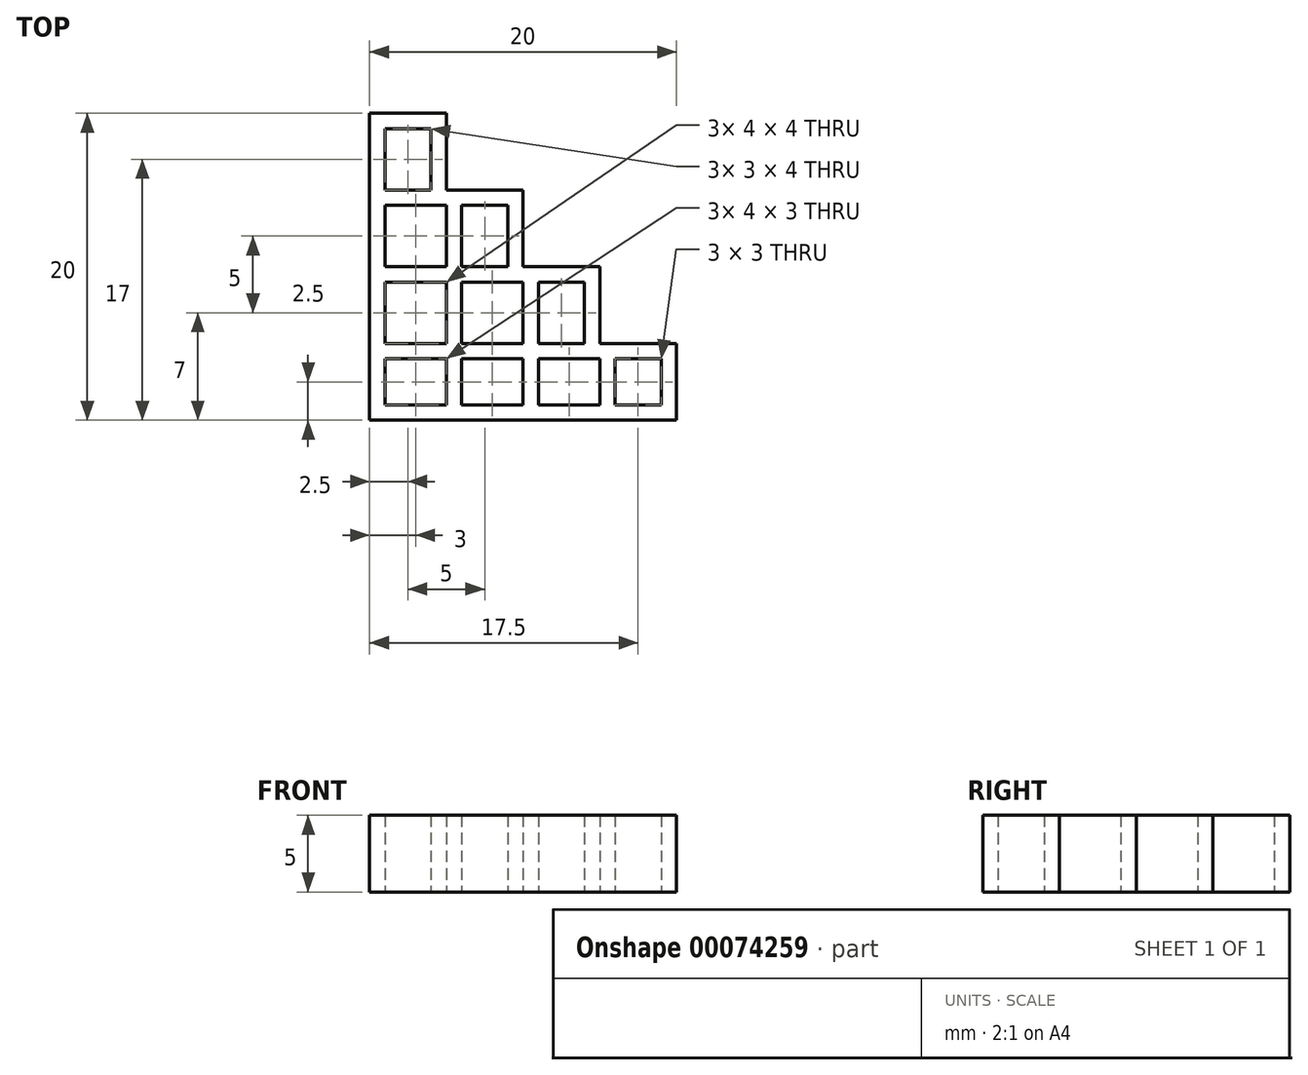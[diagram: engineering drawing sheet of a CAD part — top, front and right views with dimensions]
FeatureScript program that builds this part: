
annotation { "Feature Type Name" : "Feature", "Feature Type Description" : "" }
export const myFeature = defineFeature(function(context is Context, id is Id, definition is map)
    precondition{}
    {
        {
            var Q0;
            Q0=qCreatedBy(makeId("Top.planeOp"),FACE);
            var sketch = newSketch(context, id + "F0", { "sketchPlane" : qUnion([Q0])});
            skLineSegment(sketch, "E0.bottom", {"start": v(0, 0) * mm, "end": v(15, 0) * mm, "construction": true});
            skLineSegment(sketch, "E0.top", {"start": v(0, 10) * mm, "end": v(15, 10) * mm, "construction": true});
            skLineSegment(sketch, "E0.left", {"start": v(0, 0) * mm, "end": v(0, 10) * mm, "construction": true});
            skLineSegment(sketch, "E0.right", {"start": v(15, 0) * mm, "end": v(15, 10) * mm, "construction": true});
            skLineSegment(sketch, "E1.bottom", {"start": v(0, 0) * mm, "end": v(5, 0) * mm, "construction": true});
            skLineSegment(sketch, "E1.top", {"start": v(0, 20) * mm, "end": v(5, 20) * mm, "construction": true});
            skLineSegment(sketch, "E1.left", {"start": v(0, 0) * mm, "end": v(0, 20) * mm, "construction": true});
            skLineSegment(sketch, "E1.right", {"start": v(5, 0) * mm, "end": v(5, 20) * mm, "construction": true});
            skLineSegment(sketch, "E2.bottom", {"start": v(0, 0) * mm, "end": v(10, 0) * mm, "construction": true});
            skLineSegment(sketch, "E2.top", {"start": v(0, 15) * mm, "end": v(10, 15) * mm, "construction": true});
            skLineSegment(sketch, "E2.left", {"start": v(0, 0) * mm, "end": v(0, 15) * mm, "construction": true});
            skLineSegment(sketch, "E2.right", {"start": v(10, 0) * mm, "end": v(10, 15) * mm, "construction": true});
            skLineSegment(sketch, "E3.bottom", {"start": v(0, 0) * mm, "end": v(20, 0) * mm, "construction": true});
            skLineSegment(sketch, "E3.top", {"start": v(0, 5) * mm, "end": v(20, 5) * mm, "construction": true});
            skLineSegment(sketch, "E3.left", {"start": v(0, 0) * mm, "end": v(0, 5) * mm, "construction": true});
            skLineSegment(sketch, "E3.right", {"start": v(20, 0) * mm, "end": v(20, 5) * mm, "construction": true});
            skLineSegment(sketch, "E4", {"start": v(0, 0) * mm, "end": v(0, 20) * mm});
            skLineSegment(sketch, "E5", {"start": v(5, 20) * mm, "end": v(0, 20) * mm});
            skLineSegment(sketch, "E6", {"start": v(5, 20) * mm, "end": v(5, 15) * mm});
            skLineSegment(sketch, "E7", {"start": v(5, 15) * mm, "end": v(10, 15) * mm});
            skLineSegment(sketch, "E8", {"start": v(10, 15) * mm, "end": v(10, 10) * mm});
            skLineSegment(sketch, "E9", {"start": v(10, 10) * mm, "end": v(15, 10) * mm});
            skLineSegment(sketch, "E10", {"start": v(15, 10) * mm, "end": v(15, 5) * mm});
            skLineSegment(sketch, "E11", {"start": v(15, 5) * mm, "end": v(20, 5) * mm});
            skLineSegment(sketch, "E12", {"start": v(20, 5) * mm, "end": v(20, 0) * mm});
            skLineSegment(sketch, "E13", {"start": v(20, 0) * mm, "end": v(0, 0) * mm});
            skLineSegment(sketch, "E14", {"start": v(15, 5) * mm, "end": v(15, 0) * mm});
            skLineSegment(sketch, "E15", {"start": v(10, 10) * mm, "end": v(10, 0) * mm});
            skLineSegment(sketch, "E16", {"start": v(5, 15) * mm, "end": v(5, 0) * mm});
            skLineSegment(sketch, "E17.0", {"start": v(6, 15) * mm, "end": v(6, 0) * mm});
            skLineSegment(sketch, "E18.0", {"start": v(11, 10) * mm, "end": v(11, 0) * mm});
            skLineSegment(sketch, "E19.0", {"start": v(16, 5) * mm, "end": v(16, 0) * mm});
            skLineSegment(sketch, "E20.0", {"start": v(19, 1) * mm, "end": v(1, 1) * mm});
            skLineSegment(sketch, "E20.1", {"start": v(19, 4) * mm, "end": v(19, 1) * mm});
            skLineSegment(sketch, "E20.2", {"start": v(1, 1) * mm, "end": v(1, 19) * mm});
            skLineSegment(sketch, "E20.3", {"start": v(14, 4) * mm, "end": v(19, 4) * mm});
            skLineSegment(sketch, "E20.4", {"start": v(14, 9) * mm, "end": v(14, 4) * mm});
            skLineSegment(sketch, "E20.5", {"start": v(9, 9) * mm, "end": v(14, 9) * mm});
            skLineSegment(sketch, "E20.6", {"start": v(4, 19) * mm, "end": v(1, 19) * mm});
            skLineSegment(sketch, "E20.7", {"start": v(4, 19) * mm, "end": v(4, 14) * mm});
            skLineSegment(sketch, "E20.8", {"start": v(4, 14) * mm, "end": v(9, 14) * mm});
            skLineSegment(sketch, "E20.9", {"start": v(9, 14) * mm, "end": v(9, 9) * mm});
            skLineSegment(sketch, "E21", {"start": v(1, 15) * mm, "end": v(4, 15) * mm});
            skLineSegment(sketch, "E22", {"start": v(1, 10) * mm, "end": v(9, 10) * mm});
            skLineSegment(sketch, "E23", {"start": v(1, 5) * mm, "end": v(14, 5) * mm});
            skLineSegment(sketch, "E24.0", {"start": v(1, 14) * mm, "end": v(4, 14) * mm});
            skLineSegment(sketch, "E25.0", {"start": v(1, 9) * mm, "end": v(9, 9) * mm});
            skLineSegment(sketch, "E26.0", {"start": v(1, 4) * mm, "end": v(14, 4) * mm});
            skSolve(sketch);
        }
        {
            var Q0;
            {var subQ18=sQuery(id+"F0.wireOp",EDGE,"E4");Q0=makeQuery(id+"F0.imprint","IMPRINT",FACE,{"disambiguationData":[TD([[makeQuery(id+"F0.imprint","IMPRINT",EDGE,{"derivedFrom":subQ18}),-1.0]])]});}
            var Q1;
            {var subQ1=sQuery(id+"F0.wireOp",EDGE,"E7");var subQ3=sQuery(id+"F0.wireOp",EDGE,"E17.0");var subQ4=makeQuery(id+"F0.imprint","INTERSECT",VERTEX,{"derivedFrom":[subQ1,subQ3]});Q1=makeQuery(id+"F0.imprint","IMPRINT",FACE,{"disambiguationData":[TD([[makeQuery(id+"F0.imprint","IMPRINT",EDGE,{"disambiguationData":[TD([[subQ4,-1.0]])],"derivedFrom":subQ3}),-1.0]])]});}
            var Q2;
            {var subQ6=sQuery(id+"F0.wireOp",EDGE,"E8");Q2=makeQuery(id+"F0.imprint","IMPRINT",FACE,{"disambiguationData":[TD([[makeQuery(id+"F0.imprint","IMPRINT",EDGE,{"derivedFrom":subQ6}),-1.0]])]});}
            var Q3;
            {var subQ1=sQuery(id+"F0.wireOp",EDGE,"E9");var subQ3=sQuery(id+"F0.wireOp",EDGE,"E18.0");var subQ4=makeQuery(id+"F0.imprint","INTERSECT",VERTEX,{"derivedFrom":[subQ1,subQ3]});Q3=makeQuery(id+"F0.imprint","IMPRINT",FACE,{"disambiguationData":[TD([[makeQuery(id+"F0.imprint","IMPRINT",EDGE,{"disambiguationData":[TD([[subQ4,-1.0]])],"derivedFrom":subQ3}),-1.0]])]});}
            var Q4;
            {var subQ10=sQuery(id+"F0.wireOp",EDGE,"E10");Q4=makeQuery(id+"F0.imprint","IMPRINT",FACE,{"disambiguationData":[TD([[makeQuery(id+"F0.imprint","IMPRINT",EDGE,{"derivedFrom":subQ10}),-1.0]])]});}
            var Q5;
            {var subQ0=sQuery(id+"F0.wireOp",EDGE,"E20.5");var subQ1=sQuery(id+"F0.wireOp",EDGE,"E15");var subQ2=makeQuery(id+"F0.imprint","INTERSECT",VERTEX,{"derivedFrom":[subQ1,subQ0]});Q5=makeQuery(id+"F0.imprint","IMPRINT",FACE,{"disambiguationData":[TD([[makeQuery(id+"F0.imprint","IMPRINT",EDGE,{"disambiguationData":[TD([[subQ2,-1.0]])],"derivedFrom":subQ1}),1.0]])]});}
            var Q6;
            {var subQ0=sQuery(id+"F0.wireOp",EDGE,"E22");var subQ1=sQuery(id+"F0.wireOp",EDGE,"E16");var subQ2=makeQuery(id+"F0.imprint","INTERSECT",VERTEX,{"derivedFrom":[subQ1,subQ0]});Q6=makeQuery(id+"F0.imprint","IMPRINT",FACE,{"disambiguationData":[TD([[makeQuery(id+"F0.imprint","IMPRINT",EDGE,{"disambiguationData":[TD([[subQ2,-1.0]])],"derivedFrom":subQ1}),1.0]])]});}
            var Q7;
            {var subQ0=sQuery(id+"F0.wireOp",EDGE,"E20.8");var subQ1=sQuery(id+"F0.wireOp",EDGE,"E16");var subQ2=makeQuery(id+"F0.imprint","INTERSECT",VERTEX,{"derivedFrom":[subQ1,subQ0]});Q7=makeQuery(id+"F0.imprint","IMPRINT",FACE,{"disambiguationData":[TD([[makeQuery(id+"F0.imprint","IMPRINT",EDGE,{"disambiguationData":[TD([[subQ2,-1.0]])],"derivedFrom":subQ1}),1.0]])]});}
            var Q8;
            {var subQ0=sQuery(id+"F0.wireOp",EDGE,"E22");var subQ1=sQuery(id+"F0.wireOp",EDGE,"E16");var subQ2=makeQuery(id+"F0.imprint","INTERSECT",VERTEX,{"derivedFrom":[subQ1,subQ0]});Q8=makeQuery(id+"F0.imprint","IMPRINT",FACE,{"disambiguationData":[TD([[makeQuery(id+"F0.imprint","IMPRINT",EDGE,{"disambiguationData":[TD([[subQ2,-1.0]])],"derivedFrom":subQ1}),-1.0]])]});}
            var Q9;
            {var subQ0=sQuery(id+"F0.wireOp",EDGE,"E25.0");var subQ1=sQuery(id+"F0.wireOp",EDGE,"E16");var subQ2=makeQuery(id+"F0.imprint","INTERSECT",VERTEX,{"derivedFrom":[subQ1,subQ0]});Q9=makeQuery(id+"F0.imprint","IMPRINT",FACE,{"disambiguationData":[TD([[makeQuery(id+"F0.imprint","IMPRINT",EDGE,{"disambiguationData":[TD([[subQ2,-1.0]])],"derivedFrom":subQ1}),1.0]])]});}
            var Q10;
            {var subQ0=sQuery(id+"F0.wireOp",EDGE,"E23");var subQ1=sQuery(id+"F0.wireOp",EDGE,"E16");var subQ2=makeQuery(id+"F0.imprint","INTERSECT",VERTEX,{"derivedFrom":[subQ1,subQ0]});Q10=makeQuery(id+"F0.imprint","IMPRINT",FACE,{"disambiguationData":[TD([[makeQuery(id+"F0.imprint","IMPRINT",EDGE,{"disambiguationData":[TD([[subQ2,-1.0]])],"derivedFrom":subQ1}),-1.0]])]});}
            var Q11;
            {var subQ0=sQuery(id+"F0.wireOp",EDGE,"E26.0");var subQ1=sQuery(id+"F0.wireOp",EDGE,"E16");var subQ2=makeQuery(id+"F0.imprint","INTERSECT",VERTEX,{"derivedFrom":[subQ1,subQ0]});Q11=makeQuery(id+"F0.imprint","IMPRINT",FACE,{"disambiguationData":[TD([[makeQuery(id+"F0.imprint","IMPRINT",EDGE,{"disambiguationData":[TD([[subQ2,-1.0]])],"derivedFrom":subQ1}),1.0]])]});}
            var Q12;
            {var subQ0=sQuery(id+"F0.wireOp",EDGE,"E23");var subQ1=sQuery(id+"F0.wireOp",EDGE,"E16");var subQ2=makeQuery(id+"F0.imprint","INTERSECT",VERTEX,{"derivedFrom":[subQ1,subQ0]});Q12=makeQuery(id+"F0.imprint","IMPRINT",FACE,{"disambiguationData":[TD([[makeQuery(id+"F0.imprint","IMPRINT",EDGE,{"disambiguationData":[TD([[subQ2,-1.0]])],"derivedFrom":subQ1}),1.0]])]});}
            var Q13;
            {var subQ0=sQuery(id+"F0.wireOp",EDGE,"E16");var subQ1=sQuery(id+"F0.wireOp",EDGE,"E13");var subQ2=makeQuery(id+"F0.imprint","INTERSECT",VERTEX,{"derivedFrom":[subQ1,subQ0]});Q13=makeQuery(id+"F0.imprint","IMPRINT",FACE,{"disambiguationData":[TD([[makeQuery(id+"F0.imprint","IMPRINT",EDGE,{"disambiguationData":[TD([[subQ2,1.0]])],"derivedFrom":subQ1}),-1.0]])]});}
            var Q14;
            {var subQ0=sQuery(id+"F0.wireOp",EDGE,"E15");var subQ1=sQuery(id+"F0.wireOp",EDGE,"E13");var subQ2=makeQuery(id+"F0.imprint","INTERSECT",VERTEX,{"derivedFrom":[subQ1,subQ0]});Q14=makeQuery(id+"F0.imprint","IMPRINT",FACE,{"disambiguationData":[TD([[makeQuery(id+"F0.imprint","IMPRINT",EDGE,{"disambiguationData":[TD([[subQ2,-1.0]])],"derivedFrom":subQ1}),-1.0]])]});}
            var Q15;
            {var subQ0=sQuery(id+"F0.wireOp",EDGE,"E23");var subQ1=sQuery(id+"F0.wireOp",EDGE,"E15");var subQ2=makeQuery(id+"F0.imprint","INTERSECT",VERTEX,{"derivedFrom":[subQ1,subQ0]});Q15=makeQuery(id+"F0.imprint","IMPRINT",FACE,{"disambiguationData":[TD([[makeQuery(id+"F0.imprint","IMPRINT",EDGE,{"disambiguationData":[TD([[subQ2,-1.0]])],"derivedFrom":subQ1}),-1.0]])]});}
            var Q16;
            {var subQ0=sQuery(id+"F0.wireOp",EDGE,"E23");var subQ1=sQuery(id+"F0.wireOp",EDGE,"E15");var subQ2=makeQuery(id+"F0.imprint","INTERSECT",VERTEX,{"derivedFrom":[subQ1,subQ0]});Q16=makeQuery(id+"F0.imprint","IMPRINT",FACE,{"disambiguationData":[TD([[makeQuery(id+"F0.imprint","IMPRINT",EDGE,{"disambiguationData":[TD([[subQ2,-1.0]])],"derivedFrom":subQ1}),1.0]])]});}
            var Q17;
            {var subQ0=sQuery(id+"F0.wireOp",EDGE,"E26.0");var subQ1=sQuery(id+"F0.wireOp",EDGE,"E15");var subQ2=makeQuery(id+"F0.imprint","INTERSECT",VERTEX,{"derivedFrom":[subQ1,subQ0]});Q17=makeQuery(id+"F0.imprint","IMPRINT",FACE,{"disambiguationData":[TD([[makeQuery(id+"F0.imprint","IMPRINT",EDGE,{"disambiguationData":[TD([[subQ2,-1.0]])],"derivedFrom":subQ1}),1.0]])]});}
            var Q18;
            {var subQ0=sQuery(id+"F0.wireOp",EDGE,"E15");var subQ1=sQuery(id+"F0.wireOp",EDGE,"E13");var subQ2=makeQuery(id+"F0.imprint","INTERSECT",VERTEX,{"derivedFrom":[subQ1,subQ0]});Q18=makeQuery(id+"F0.imprint","IMPRINT",FACE,{"disambiguationData":[TD([[makeQuery(id+"F0.imprint","IMPRINT",EDGE,{"disambiguationData":[TD([[subQ2,1.0]])],"derivedFrom":subQ1}),-1.0]])]});}
            var Q19;
            {var subQ0=sQuery(id+"F0.wireOp",EDGE,"E14");var subQ1=sQuery(id+"F0.wireOp",EDGE,"E13");var subQ2=makeQuery(id+"F0.imprint","INTERSECT",VERTEX,{"derivedFrom":[subQ1,subQ0]});Q19=makeQuery(id+"F0.imprint","IMPRINT",FACE,{"disambiguationData":[TD([[makeQuery(id+"F0.imprint","IMPRINT",EDGE,{"disambiguationData":[TD([[subQ2,-1.0]])],"derivedFrom":subQ1}),-1.0]])]});}
            var Q20;
            {var subQ0=sQuery(id+"F0.wireOp",EDGE,"E23");var subQ1=sQuery(id+"F0.wireOp",EDGE,"E18.0");var subQ2=makeQuery(id+"F0.imprint","INTERSECT",VERTEX,{"derivedFrom":[subQ1,subQ0]});Q20=makeQuery(id+"F0.imprint","IMPRINT",FACE,{"disambiguationData":[TD([[makeQuery(id+"F0.imprint","IMPRINT",EDGE,{"disambiguationData":[TD([[subQ2,-1.0]])],"derivedFrom":subQ1}),1.0]])]});}
            var Q21;
            {var subQ1=sQuery(id+"F0.wireOp",EDGE,"E11");var subQ3=sQuery(id+"F0.wireOp",EDGE,"E19.0");var subQ4=makeQuery(id+"F0.imprint","INTERSECT",VERTEX,{"derivedFrom":[subQ1,subQ3]});Q21=makeQuery(id+"F0.imprint","IMPRINT",FACE,{"disambiguationData":[TD([[makeQuery(id+"F0.imprint","IMPRINT",EDGE,{"disambiguationData":[TD([[subQ4,-1.0]])],"derivedFrom":subQ3}),-1.0]])]});}
            var Q22;
            {var subQ0=sQuery(id+"F0.wireOp",EDGE,"E20.3");var subQ1=sQuery(id+"F0.wireOp",EDGE,"E14");var subQ2=makeQuery(id+"F0.imprint","INTERSECT",VERTEX,{"derivedFrom":[subQ1,subQ0]});Q22=makeQuery(id+"F0.imprint","IMPRINT",FACE,{"disambiguationData":[TD([[makeQuery(id+"F0.imprint","IMPRINT",EDGE,{"disambiguationData":[TD([[subQ2,-1.0]])],"derivedFrom":subQ1}),1.0]])]});}
            var Q23;
            {var subQ0=sQuery(id+"F0.wireOp",EDGE,"E14");var subQ1=sQuery(id+"F0.wireOp",EDGE,"E13");var subQ2=makeQuery(id+"F0.imprint","INTERSECT",VERTEX,{"derivedFrom":[subQ1,subQ0]});Q23=makeQuery(id+"F0.imprint","IMPRINT",FACE,{"disambiguationData":[TD([[makeQuery(id+"F0.imprint","IMPRINT",EDGE,{"disambiguationData":[TD([[subQ2,1.0]])],"derivedFrom":subQ1}),-1.0]])]});}
            var Q24;
            {var subQ6=sQuery(id+"F0.wireOp",EDGE,"E12");Q24=makeQuery(id+"F0.imprint","IMPRINT",FACE,{"disambiguationData":[TD([[makeQuery(id+"F0.imprint","IMPRINT",EDGE,{"derivedFrom":subQ6}),-1.0]])]});}
            var Q25;
            {var subQ0=sQuery(id+"F0.wireOp",EDGE,"E22");var subQ1=sQuery(id+"F0.wireOp",EDGE,"E17.0");var subQ2=makeQuery(id+"F0.imprint","INTERSECT",VERTEX,{"derivedFrom":[subQ1,subQ0]});Q25=makeQuery(id+"F0.imprint","IMPRINT",FACE,{"disambiguationData":[TD([[makeQuery(id+"F0.imprint","IMPRINT",EDGE,{"disambiguationData":[TD([[subQ2,-1.0]])],"derivedFrom":subQ1}),1.0]])]});}
            var Q26;
            {var subQ0=sQuery(id+"F0.wireOp",EDGE,"E21");Q26=makeQuery(id+"F0.imprint","IMPRINT",FACE,{"disambiguationData":[TD([[makeQuery(id+"F0.imprint","IMPRINT",EDGE,{"derivedFrom":subQ0}),-1.0]])]});}
            extrude(context, id + "F1", {"entities" : qUnion([Q0, Q1, Q2, Q3, Q4, Q5, Q6, Q7, Q8, Q9, Q10, Q11, Q12, Q13, Q14, Q15, Q16, Q17, Q18, Q19, Q20, Q21, Q22, Q23, Q24, Q25, Q26]), "depth" : 5 * mm});
        }
    });
